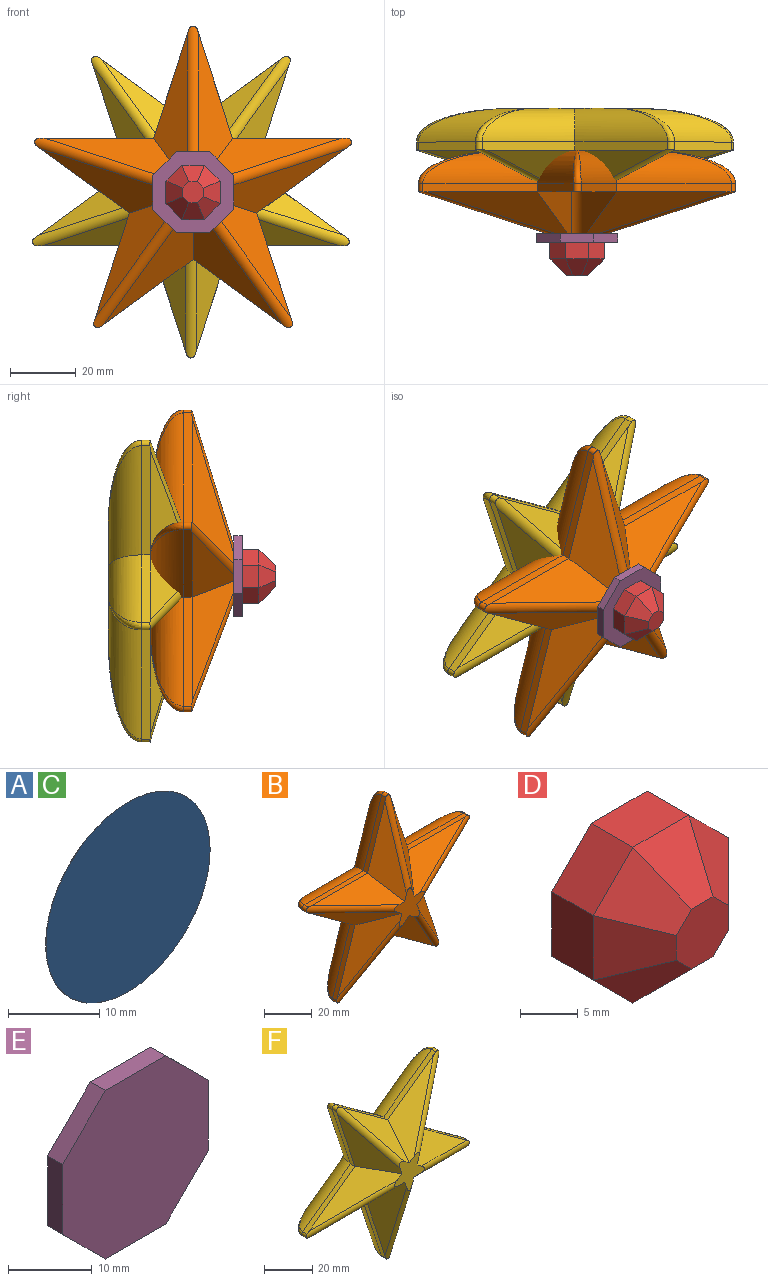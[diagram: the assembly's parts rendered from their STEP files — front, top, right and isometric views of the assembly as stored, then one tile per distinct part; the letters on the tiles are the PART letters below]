
ASSEMBLY  parts=6 mates=5
PART A: 3 faces, bbox 25.4x0x25.4 mm
  f0: cylinder r=12.7mm len=25.4mm, axis (0,1,0), area 2mm2, adj f1,f2
  f1: plane 25.4x25.4mm, normal (0,-1,0), area 506.7mm2, adj f0
  f2: plane 25.4x25.4mm, normal (0,1,0), area 506.7mm2, adj f0
PART B: 47 faces, bbox 101.6x26x96.6 mm
  f0: plane 33.19x10.78mm, normal (-0.95,0,0.31), area 88.6mm2, adj f1,f16,f22,f29,f44
  f1: plane 34.9x2.54mm, normal (0,0,1), area 88.6mm2, adj f0,f14,f24,f28,f42
  f2: plane 28.23x20.51mm, normal (-0.59,0,-0.81), area 88.6mm2, adj f3,f12,f24,f28,f38
  f3: plane 33.19x10.78mm, normal (-0.95,0,0.31), area 88.6mm2, adj f2,f13,f25,f30,f36
  f4: plane 28.23x20.51mm, normal (0.59,0,-0.81), area 88.6mm2, adj f5,f15,f25,f30,f32
  f5: plane 28.23x20.51mm, normal (-0.59,0,-0.81), area 88.6mm2, adj f4,f17,f23,f31,f33
  f6: plane 33.19x10.78mm, normal (0.95,0,0.31), area 88.6mm2, adj f7,f19,f23,f31,f37
  f7: plane 28.23x20.51mm, normal (0.59,0,-0.81), area 88.6mm2, adj f6,f21,f26,f27,f39
  f8: plane 34.9x2.54mm, normal (0,0,1), area 88.6mm2, adj f9,f20,f26,f27,f43
  f9: plane 33.19x10.78mm, normal (0.95,0,0.31), area 88.6mm2, adj f8,f18,f22,f29,f45
  f10: plane 17.76x16.97mm, normal (0,-1,0), area 151.6mm2, adj f12,f13,f14,f15,f16,f17,f18,f19
  f11: plane 39.06x37.15mm, normal (0,1,0), area 473.4mm2, adj f32,f33,f36,f37,f38,f39,f42,f43
  f12: plane 41.85x19.56mm, normal (-0.42,-0.71,-0.57), area 329.6mm2, adj f2,f10,f13,f28
  f13: plane 36.5x25.21mm, normal (-0.67,-0.71,0.22), area 329.6mm2, adj f3,f10,f12,f30
  f14: plane 42.51x12.7mm, normal (0,-0.71,0.71), area 329.6mm2, adj f1,f10,f16,f28
  f15: plane 35.26x26.92mm, normal (0.42,-0.71,-0.57), area 329.6mm2, adj f4,f10,f17,f30
  f16: plane 44.35x12.7mm, normal (-0.67,-0.71,0.22), area 329.6mm2, adj f0,f10,f14,f29
  f17: plane 35.26x26.92mm, normal (-0.42,-0.71,-0.57), area 329.6mm2, adj f5,f10,f15,f31
  f18: plane 44.35x12.7mm, normal (0.67,-0.71,0.22), area 329.6mm2, adj f9,f10,f20,f29
  f19: plane 36.5x25.21mm, normal (0.67,-0.71,0.22), area 329.6mm2, adj f6,f10,f21,f31
  f20: plane 42.51x12.7mm, normal (0,-0.71,0.71), area 329.6mm2, adj f8,f10,f18,f27
  f21: plane 41.85x19.56mm, normal (0.42,-0.71,-0.57), area 329.6mm2, adj f7,f10,f19,f27
  f22: cylinder r=1.27mm len=2.48mm, axis (0,1,0), area 7.8mm2, adj f0,f9,f29,f46
  f23: cylinder r=1.27mm len=2.48mm, axis (0,-1,0), area 7.8mm2, adj f5,f6,f31,f35
  f24: cylinder r=1.27mm len=2.48mm, axis (0,1,0), area 7.8mm2, adj f1,f2,f28,f40
  f25: cylinder r=1.27mm len=2.48mm, axis (0,-1,0), area 7.8mm2, adj f3,f4,f30,f34
  f26: cylinder r=1.27mm len=2.48mm, axis (0,1,0), area 7.8mm2, adj f7,f8,f27,f41
  f27: cylinder r=2.54mm len=42.26mm, axis (-0.91,-0.3,-0.3), area 162.1mm2, adj f7,f8,f10,f20,f21,f26
  f28: cylinder r=2.54mm len=42.26mm, axis (0.91,-0.3,-0.3), area 162.1mm2, adj f1,f2,f10,f12,f14,f24
  f29: cylinder r=2.54mm len=43.52mm, axis (0,-0.3,-0.96), area 162.1mm2, adj f0,f9,f10,f16,f18,f22
  f30: cylinder r=2.54mm len=37.06mm, axis (0.56,-0.3,0.77), area 162.1mm2, adj f3,f4,f10,f13,f15,f25
  f31: cylinder r=2.54mm len=37.06mm, axis (-0.56,-0.3,0.77), area 162.1mm2, adj f5,f6,f10,f17,f19,f23
  f32: cylinder r=10.16mm len=40.18mm, axis (0.81,0,0.59), area 441.1mm2, adj f4,f11,f33,f34
  f33: cylinder r=10.16mm len=40.18mm, axis (0.81,0,-0.59), area 441.1mm2, adj f5,f11,f32,f35
  f34: bspline ~26.6x19.33mm, area 50.9mm2, adj f25,f32,f36
  f35: bspline ~26.6x19.33mm, area 50.9mm2, adj f23,f33,f37
  f36: cylinder r=10.16mm len=43.35mm, axis (-0.31,0,-0.95), area 441.1mm2, adj f3,f11,f34,f38
  f37: cylinder r=10.16mm len=43.35mm, axis (-0.31,0,0.95), area 441.1mm2, adj f6,f11,f35,f39
  f38: cylinder r=10.16mm len=40.18mm, axis (0.81,0,-0.59), area 441.1mm2, adj f2,f11,f36,f40
  f39: cylinder r=10.16mm len=40.18mm, axis (0.81,0,0.59), area 441.1mm2, adj f7,f11,f37,f41
  f40: bspline ~31.27x12.87mm, area 50.9mm2, adj f24,f38,f42
  f41: bspline ~31.27x12.87mm, area 50.9mm2, adj f26,f39,f43
  f42: cylinder r=10.16mm len=42.28mm, axis (-1,0,0), area 441.1mm2, adj f1,f11,f40,f44
  f43: cylinder r=10.16mm len=42.28mm, axis (-1,0,0), area 441.1mm2, adj f8,f11,f41,f45
  f44: cylinder r=10.16mm len=43.35mm, axis (-0.31,0,-0.95), area 441.1mm2, adj f0,f11,f42,f46
  f45: cylinder r=10.16mm len=43.35mm, axis (-0.31,0,0.95), area 441.1mm2, adj f9,f11,f43,f46
  f46: bspline ~32.88x12.87mm, area 50.9mm2, adj f22,f44,f45
PART C: same geometry as A
PART D: 18 faces, bbox 16.5x10.2x16.5 mm
  f0: plane 5.08x4.84mm, normal (-0.71,0,0.71), area 34.7mm2, adj f1,f7,f9,f17
  f1: plane 6.84x5.08mm, normal (-1,0,0), area 34.7mm2, adj f0,f2,f9,f15
  f2: plane 5.08x4.84mm, normal (-0.71,0,-0.71), area 34.7mm2, adj f1,f3,f9,f13
  f3: plane 6.84x5.08mm, normal (0,0,-1), area 34.7mm2, adj f2,f4,f9,f11
  f4: plane 5.08x4.84mm, normal (0.71,0,-0.71), area 34.7mm2, adj f3,f5,f9,f10
  f5: plane 6.84x5.08mm, normal (1,0,0), area 34.7mm2, adj f4,f6,f9,f12
  f6: plane 5.08x4.84mm, normal (0.71,0,0.71), area 34.7mm2, adj f5,f7,f9,f14
  f7: plane 6.84x5.08mm, normal (0,0,1), area 34.7mm2, adj f0,f6,f9,f16
  f8: plane 6.35x6.35mm, normal (0,-1,0), area 33.4mm2, adj f10,f11,f12,f13,f14,f15,f16,f17
  f9: plane 16.51x16.51mm, normal (0,1,0), area 225.8mm2, adj f0,f1,f2,f3,f4,f5,f6,f7
  f10: plane 6.94x6.94mm, normal (0.5,-0.71,-0.5), area 34mm2, adj f4,f8,f11,f12
  f11: plane 6.84x5.08mm, normal (0,-0.71,-0.71), area 34mm2, adj f3,f8,f10,f13
  f12: plane 6.84x5.08mm, normal (0.71,-0.71,0), area 34mm2, adj f5,f8,f10,f14
  f13: plane 6.94x6.94mm, normal (-0.5,-0.71,-0.5), area 34mm2, adj f2,f8,f11,f15
  f14: plane 6.94x6.94mm, normal (0.5,-0.71,0.5), area 34mm2, adj f6,f8,f12,f16
  f15: plane 6.84x5.08mm, normal (-0.71,-0.71,0), area 34mm2, adj f1,f8,f13,f17
  f16: plane 6.84x5.08mm, normal (0,-0.71,0.71), area 34mm2, adj f7,f8,f14,f17
  f17: plane 6.94x6.94mm, normal (-0.5,-0.71,0.5), area 34mm2, adj f0,f8,f15,f16
PART E: 10 faces, bbox 24.6x2.5x24.6 mm
  f0: plane 10.2x2.54mm, normal (0,0,1), area 25.9mm2, adj f1,f7,f8,f9
  f1: plane 7.21x7.21mm, normal (-0.71,0,0.71), area 25.9mm2, adj f0,f2,f8,f9
  f2: plane 10.2x2.54mm, normal (-1,0,0), area 25.9mm2, adj f1,f3,f8,f9
  f3: plane 7.21x7.21mm, normal (-0.71,0,-0.71), area 25.9mm2, adj f2,f4,f8,f9
  f4: plane 10.2x2.54mm, normal (0,0,-1), area 25.9mm2, adj f3,f5,f8,f9
  f5: plane 7.21x7.21mm, normal (0.71,0,-0.71), area 25.9mm2, adj f4,f6,f8,f9
  f6: plane 10.2x2.54mm, normal (1,0,0), area 25.9mm2, adj f5,f7,f8,f9
  f7: plane 7.21x7.21mm, normal (0.71,0,0.71), area 25.9mm2, adj f0,f6,f8,f9
  f8: plane 24.63x24.63mm, normal (0,-1,0), area 502.7mm2, adj f0,f1,f2,f3,f4,f5,f6,f7
  f9: plane 24.63x24.63mm, normal (0,1,0), area 502.7mm2, adj f0,f1,f2,f3,f4,f5,f6,f7
PART F: 47 faces, bbox 101.6x26x96.6 mm
  f0: plane 34.9x2.54mm, normal (0,0,-1), area 88.6mm2, adj f1,f14,f22,f29,f44
  f1: plane 33.19x10.78mm, normal (-0.95,0,-0.31), area 88.6mm2, adj f0,f16,f24,f30,f42
  f2: plane 33.19x10.78mm, normal (0.95,0,-0.31), area 88.6mm2, adj f3,f18,f24,f30,f38
  f3: plane 34.9x2.54mm, normal (0,0,-1), area 88.6mm2, adj f2,f20,f26,f31,f36
  f4: plane 28.23x20.51mm, normal (0.59,0,0.81), area 88.6mm2, adj f5,f21,f26,f31,f32
  f5: plane 33.19x10.78mm, normal (0.95,0,-0.31), area 88.6mm2, adj f4,f19,f23,f28,f33
  f6: plane 28.23x20.51mm, normal (-0.59,0,0.81), area 88.6mm2, adj f7,f17,f23,f28,f37
  f7: plane 28.23x20.51mm, normal (0.59,0,0.81), area 88.6mm2, adj f6,f15,f25,f27,f39
  f8: plane 33.19x10.78mm, normal (-0.95,0,-0.31), area 88.6mm2, adj f9,f13,f25,f27,f43
  f9: plane 28.23x20.51mm, normal (-0.59,0,0.81), area 88.6mm2, adj f8,f12,f22,f29,f45
  f10: plane 17.76x16.97mm, normal (0,-1,0), area 151.6mm2, adj f12,f13,f14,f15,f16,f17,f18,f19
  f11: plane 39.06x37.15mm, normal (0,1,0), area 473.4mm2, adj f32,f33,f36,f37,f38,f39,f42,f43
  f12: plane 41.85x19.56mm, normal (-0.42,-0.71,0.57), area 329.6mm2, adj f9,f10,f13,f29
  f13: plane 36.5x25.21mm, normal (-0.67,-0.71,-0.22), area 329.6mm2, adj f8,f10,f12,f27
  f14: plane 42.51x12.7mm, normal (0,-0.71,-0.71), area 329.6mm2, adj f0,f10,f16,f29
  f15: plane 35.26x26.92mm, normal (0.42,-0.71,0.57), area 329.6mm2, adj f7,f10,f17,f27
  f16: plane 44.35x12.7mm, normal (-0.67,-0.71,-0.22), area 329.6mm2, adj f1,f10,f14,f30
  f17: plane 35.26x26.92mm, normal (-0.42,-0.71,0.57), area 329.6mm2, adj f6,f10,f15,f28
  f18: plane 44.35x12.7mm, normal (0.67,-0.71,-0.22), area 329.6mm2, adj f2,f10,f20,f30
  f19: plane 36.5x25.21mm, normal (0.67,-0.71,-0.22), area 329.6mm2, adj f5,f10,f21,f28
  f20: plane 42.51x12.7mm, normal (0,-0.71,-0.71), area 329.6mm2, adj f3,f10,f18,f31
  f21: plane 41.85x19.56mm, normal (0.42,-0.71,0.57), area 329.6mm2, adj f4,f10,f19,f31
  f22: cylinder r=1.27mm len=2.48mm, axis (0,1,0), area 7.8mm2, adj f0,f9,f29,f46
  f23: cylinder r=1.27mm len=2.48mm, axis (0,1,0), area 7.8mm2, adj f5,f6,f28,f35
  f24: cylinder r=1.27mm len=2.48mm, axis (0,1,0), area 7.8mm2, adj f1,f2,f30,f40
  f25: cylinder r=1.27mm len=2.48mm, axis (0,1,0), area 7.8mm2, adj f7,f8,f27,f41
  f26: cylinder r=1.27mm len=2.48mm, axis (0,1,0), area 7.8mm2, adj f3,f4,f31,f34
  f27: cylinder r=2.54mm len=37.06mm, axis (0.56,-0.3,-0.77), area 162.1mm2, adj f7,f8,f10,f13,f15,f25
  f28: cylinder r=2.54mm len=37.06mm, axis (-0.56,-0.3,-0.77), area 162.1mm2, adj f5,f6,f10,f17,f19,f23
  f29: cylinder r=2.54mm len=42.26mm, axis (-0.91,0.3,-0.3), area 162.1mm2, adj f0,f9,f10,f12,f14,f22
  f30: cylinder r=2.54mm len=43.52mm, axis (0,0.3,-0.96), area 162.1mm2, adj f1,f2,f10,f16,f18,f24
  f31: cylinder r=2.54mm len=42.26mm, axis (0.91,0.3,-0.3), area 162.1mm2, adj f3,f4,f10,f20,f21,f26
  f32: cylinder r=10.16mm len=40.18mm, axis (-0.81,0,0.59), area 441.1mm2, adj f4,f11,f33,f34
  f33: cylinder r=10.16mm len=43.35mm, axis (0.31,0,0.95), area 441.1mm2, adj f5,f11,f32,f35
  f34: bspline ~31.27x12.87mm, area 50.9mm2, adj f26,f32,f36
  f35: bspline ~26.6x19.33mm, area 50.9mm2, adj f23,f33,f37
  f36: cylinder r=10.16mm len=42.28mm, axis (1,0,0), area 441.1mm2, adj f3,f11,f34,f38
  f37: cylinder r=10.16mm len=40.18mm, axis (-0.81,0,-0.59), area 441.1mm2, adj f6,f11,f35,f39
  f38: cylinder r=10.16mm len=43.35mm, axis (0.31,0,0.95), area 441.1mm2, adj f2,f11,f36,f40
  f39: cylinder r=10.16mm len=40.18mm, axis (-0.81,0,0.59), area 441.1mm2, adj f7,f11,f37,f41
  f40: bspline ~32.88x12.87mm, area 50.9mm2, adj f24,f38,f42
  f41: bspline ~26.6x19.33mm, area 50.9mm2, adj f25,f39,f43
  f42: cylinder r=10.16mm len=43.35mm, axis (0.31,0,-0.95), area 441.1mm2, adj f1,f11,f40,f44
  f43: cylinder r=10.16mm len=43.35mm, axis (0.31,0,-0.95), area 441.1mm2, adj f8,f11,f41,f45
  f44: cylinder r=10.16mm len=42.28mm, axis (1,0,0), area 441.1mm2, adj f0,f11,f42,f46
  f45: cylinder r=10.16mm len=40.18mm, axis (-0.81,0,-0.59), area 441.1mm2, adj f9,f11,f43,f46
  f46: bspline ~31.27x12.87mm, area 50.9mm2, adj f22,f44,f45
PLACE A t=(22.56,38.44,10.42)mm
PLACE B rot(axis=(1,0,0),0deg) t=(23.22,25.72,10.21)mm
PLACE C rot(axis=(0,-1,0),180deg) t=(23.22,13.04,10.21)mm
PLACE D rot(axis=(1,0,0),0deg) t=(80.6,-2.22,52.54)mm
PLACE E rot(axis=(1,0,0),0deg) t=(23.22,25.72,10.21)mm
PLACE F t=(22.56,38.42,10.42)mm
MATE revolute F.f11 <-> A.f0  axis (0,1,0) through (22.56,38.42,10.42)mm
MATE revolute C.f0 <-> F.f10  axis (0,-1,0) through (23.22,13.02,10.21)mm
MATE revolute B.f11 <-> C.f0  axis (0,1,0) through (23.22,25.72,10.21)mm
MATE revolute E.f9 <-> B.f10  axis (0,1,0) through (23.22,0.32,10.21)mm
MATE revolute D.f9 <-> E.f8  axis (0,1,0) through (23.22,-2.22,10.21)mm
